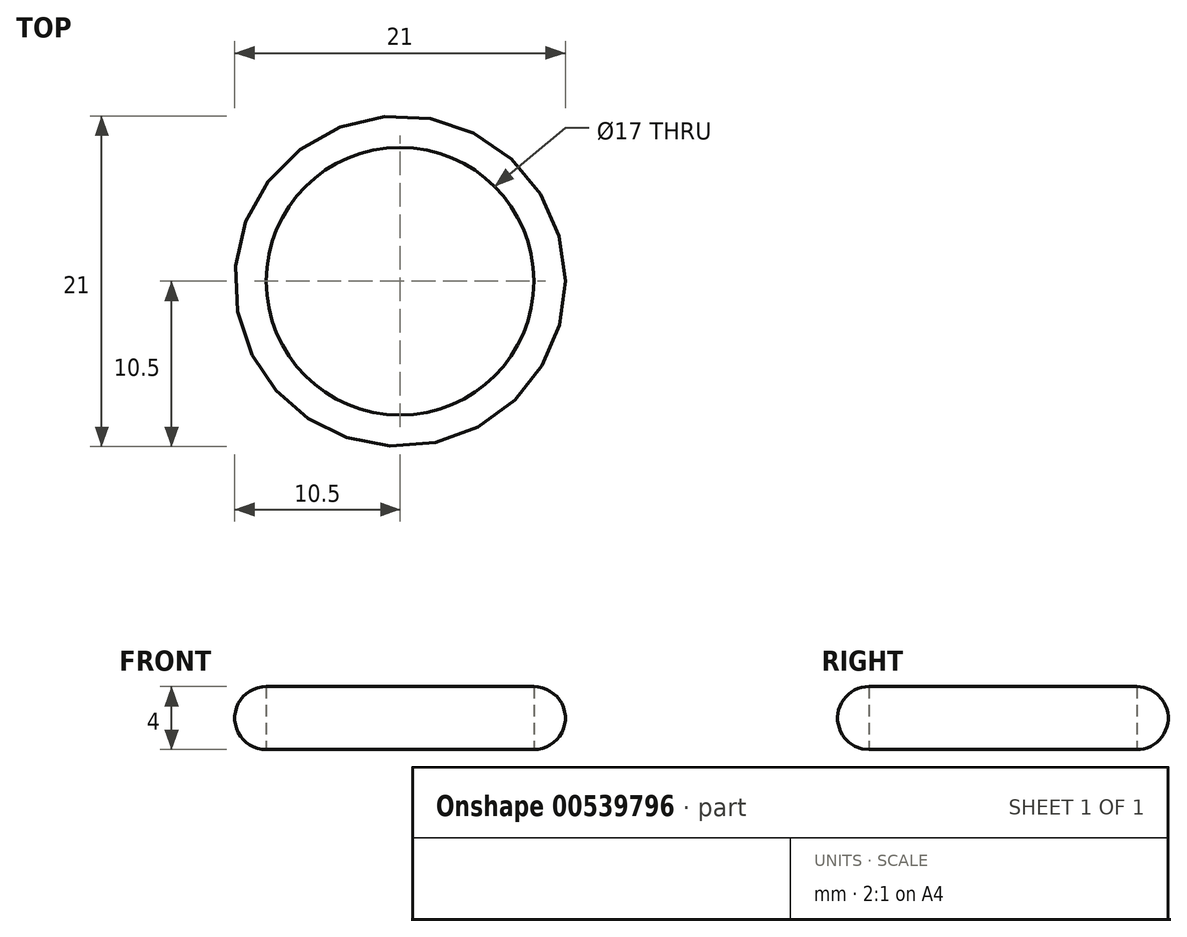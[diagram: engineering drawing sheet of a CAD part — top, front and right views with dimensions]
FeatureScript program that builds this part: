
annotation { "Feature Type Name" : "Feature", "Feature Type Description" : "" }
export const myFeature = defineFeature(function(context is Context, id is Id, definition is map)
    precondition{}
    {
        {
            var Q0;
            Q0=qCreatedBy(makeId("Top.planeOp"),FACE);
            var sketch = newSketch(context, id + "F0", { "sketchPlane" : qUnion([Q0])});
            skCircle(sketch, "E0", {"center": v(0, 0) * mm, "radius": 10.5 * mm});
            skCircle(sketch, "E1", {"center": v(0, 0) * mm, "radius": 8.5 * mm});
            skSolve(sketch);
        }
        {
            var Q0;
            Q0 = qSketchRegion(id + "F0", true);
            extrude(context, id + "F1", {"entities" : qUnion([Q0]), "depth" : 4 * mm, "offsetDistance" : 25 * mm});
        }
        {
            var Q0;
            Q0=makeQuery(id+"F1.opExtrude","CAP_EDGE",EDGE,{"disambiguationData":[OSD([sQuery(id+"F0.wireOp",EDGE,"E0")])],"isStart":false});
            var Q1;
            Q1=makeQuery(id+"F1.opExtrude","CAP_EDGE",EDGE,{"disambiguationData":[OSD([sQuery(id+"F0.wireOp",EDGE,"E0")])],"isStart":true});
            fillet(context, id + "F2", {"entities" : qUnion([Q0, Q1]), "radius" : 2 * mm, "tangentPropagation" : true, "allowEdgeOverflow" : false});
        }
    });
